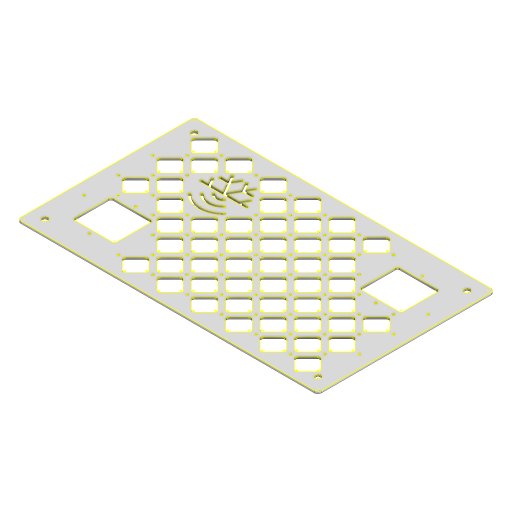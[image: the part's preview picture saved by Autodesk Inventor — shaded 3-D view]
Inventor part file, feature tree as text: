
AUTODESK INVENTOR PART (.ipt)
format: ipt  version: 2023 (Build 270158000, 158)  size: 2,629,120 bytes
history: native  units: mm
features: other x15, extrude x9, sketch x8, fillet x4, projected_geometry x2
ambient origin geometry x8: Origin, YZ Plane, XZ Plane, XY Plane, X Axis, Y Axis, Z Axis, Center Point
bodies: Solid1 (feature_tree)
feature tree (38):
  other  "Blocks"
  extrude  "Extrusion1"  Depth=216.805mm
  extrude  "Extrusion2"  Depth=20.0mm
  fillet  "Fillet1"  Radius=20.0mm
  sketch  "Sketch3"  dims[d12=20.0mm d13=20.0mm]
  extrude  "Mount Hole Center"  Depth=20.0mm
  extrude  "Octagon N"  Depth=3.175mm TaperAngle=0.0deg
  fillet  "Octagon N Filet"  Radius=56.0mm
  extrude  "Octagon E"  Depth=40.0mm
  fillet  "Octagon E Filet"  Radius=40.0mm
  extrude  "Mount Hole NE"  Depth=3.3mm
  sketch  "Sketch4"  dims[d14=8.73125mm d15=3.175mm d16=0.0mm d17=56.0mm]
  other  "Mount Hole Center Pattern"
  other  "Mount Hole NE Pattern"
  other  "Octagon N Pattern"
  other  "Octagon E Pattern"
  fillet  "Fillet4"  Radius=68.0mm
  extrude  "Extrusion8"  Depth=30.5mm
  extrude  "Extrusion10"  TaperAngle=0.0deg  [1 undecoded]
  extrude  "Extrusion11"  Depth=3.0mm
  sketch  "Sketch21"  dims[d28=20.0mm d30=360.0deg d32=0.0mm d33=0.0mm d34=3.0mm d35=50.0mm d36=14.644661mm d37=4.0mm d38=4.0mm d39=4.0mm d40=4.0mm d41=3.3mm d42=4.0mm d43=4.0mm d44=4.0mm d45=4.0mm d46=3.3mm d47=25.0mm d48=25.0mm d49=0.0mm d50=0.0mm d51=0.0mm d52=0.0mm d53=2.0mm d54=0.0mm d55=0.0mm d56=2.0mm d57=0.0mm d58=0.0mm d59=200.0mm d60=100.0mm d61=90.0mm d63=50.0mm d64=50.0mm d66=50.0mm d71=5.0mm d72=0.0mm d73=0.0mm d76=0.0mm d77=0.0mm d79=69.342146mm d83=69.97714mm d84=15.328927mm d85=15.01143mm d86=3.75mm d87=60.0deg d89=120.0deg d90=3.75mm d91=3.75mm d94=60.0deg d95=3.75mm d96=11.75mm d102=60.0deg d103=3.75mm d105=90.0deg d106=3.75mm d107=45.0deg d108=90.0deg d109=3.75mm d110=90.0deg d111=3.75mm d112=10.0mm d113=0.0mm]
  sketch  "Sketch1"  dims[d0=20.0mm d2=396.657mm d3=20.0mm d5=216.805mm d8=198.3285mm]
  sketch  "Sketch2"  dims[d9=108.4025mm d10=20.0mm d11=20.0mm]
  projected_geometry  "Projected Loop1"
  other  "logo"
  other  "logo2"
  other  "logo3"
  sketch  "Sketch8"  dims[d18=61.0mm d19=40.0mm d20=40.0mm]
  other  "Block4"
  other  "Block5"
  other  "Block6"
  sketch  "Sketch18"  dims[d21=3.3mm d22=3.3mm d23=68.0mm]
  other  "Block7"
  sketch  "Sketch20"  dims[d24=34.0mm d27=30.5mm]
  other  "Image1"
  projected_geometry  "Projected Loop9"
  other  "Block4:1"
  other  "Block7:1"
note: 1 required parameter value undecoded (feature->parameter linkage not recoverable at this tier; creation-order binding heuristic only, values carry confidence <= 0.55)
